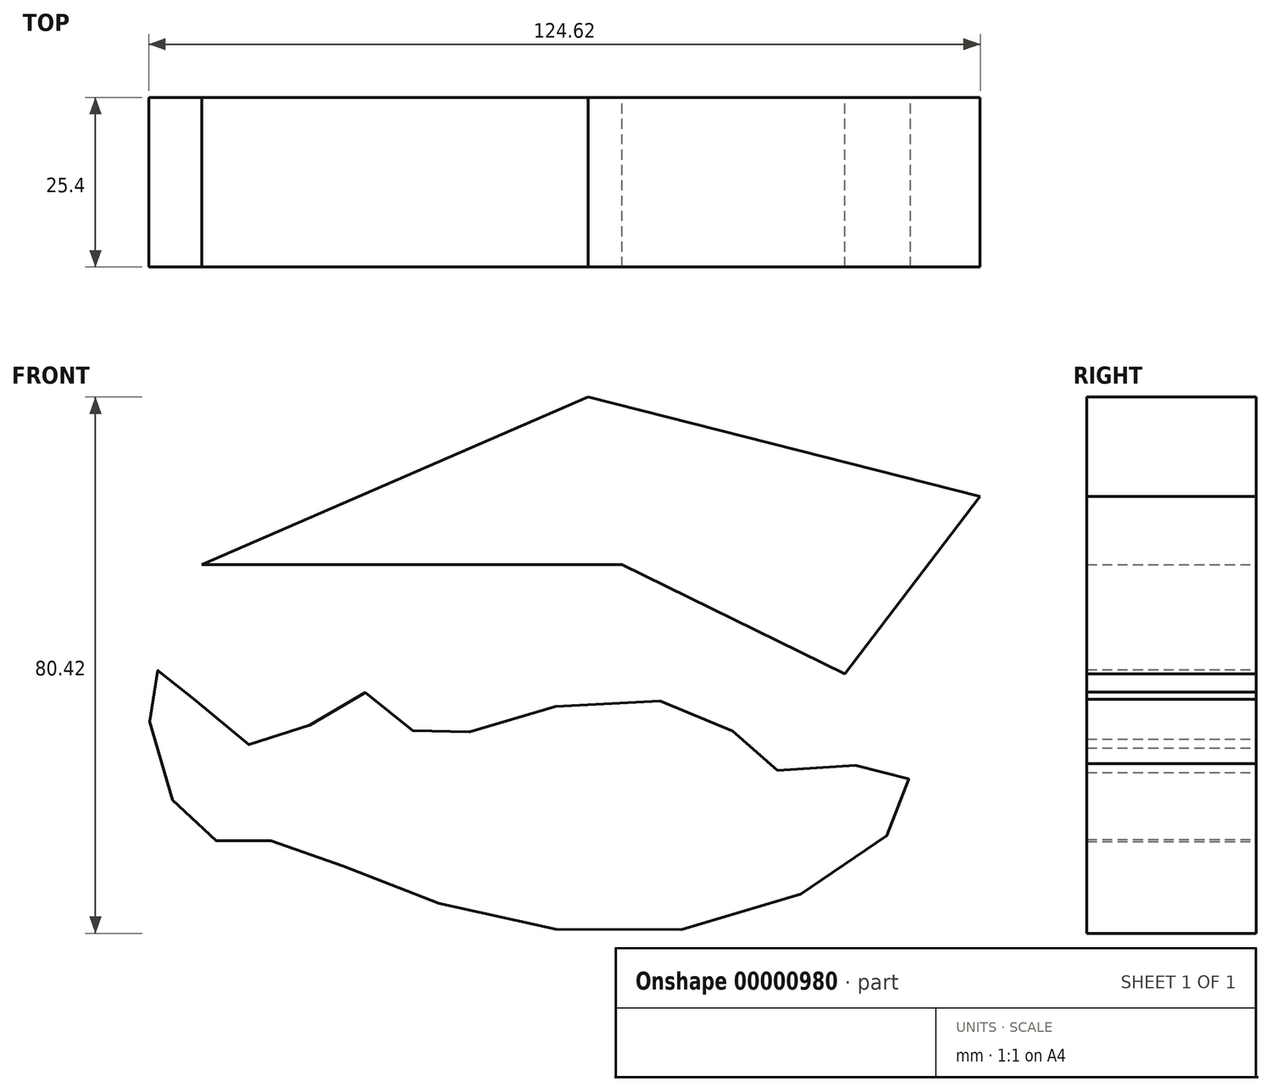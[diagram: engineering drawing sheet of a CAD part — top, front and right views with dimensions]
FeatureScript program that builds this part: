
annotation { "Feature Type Name" : "Feature", "Feature Type Description" : "" }
export const myFeature = defineFeature(function(context is Context, id is Id, definition is map)
    precondition{}
    {
        {
            var Q0;
            Q0=qCreatedBy(makeId("Front.planeOp"),FACE);
            var sketch = newSketch(context, id + "F0", { "sketchPlane" : qUnion([Q0])});
            skLineSegment(sketch, "E0", {"start": v(-57.86, 36.5) * mm, "end": v(5.1, 36.5) * mm});
            skLineSegment(sketch, "E1", {"start": v(5.1, 36.5) * mm, "end": v(38.54, 20.14) * mm});
            skLineSegment(sketch, "E2", {"start": v(38.54, 20.14) * mm, "end": v(58.8, 46.74) * mm});
            skLineSegment(sketch, "E3", {"start": v(58.8, 46.74) * mm, "end": v(0, 61.63) * mm});
            skLineSegment(sketch, "E4", {"start": v(0, 61.63) * mm, "end": v(-57.86, 36.5) * mm});
            skFitSpline(sketch, "E5", {"points": [v(-59.03, 16.3) * mm, v(-47.07, 9.13) * mm, v(-34.24, 17.4) * mm, v(-25.11, 10.87) * mm, v(-10.54, 13.91) * mm, v(19.02, 13.7) * mm, v(28.37, 5.65) * mm, v(45.98, 6.3) * mm, v(47.72, 0) * mm, v(18.8, -17.4) * mm, v(-27.29, -12.61) * mm, v(-48.6, -4.78) * mm, v(-57.5, -4.35) * mm, v(-65.33, 10.44) * mm, v(-64.46, 20.65) * mm, v(-59.03, 16.3) * mm]});
            skSolve(sketch);
        }
        {
            var Q0;
            Q0=makeQuery(id+"F0.imprint","IMPRINT",FACE,{"disambiguationData":[TD([[makeQuery(id+"F0.imprint","IMPRINT",EDGE,{"derivedFrom":sQuery(id+"F0.wireOp",EDGE,"E0")}),1.0]])]});
            var Q1;
            Q1=makeQuery(id+"F0.imprint","IMPRINT",FACE,{"disambiguationData":[TD([[makeQuery(id+"F0.imprint","IMPRINT",EDGE,{"derivedFrom":sQuery(id+"F0.wireOp",EDGE,"E5")}),-1.0]])]});
            extrude(context, id + "F1", {"entities" : qUnion([Q0, Q1]), "depth" : 25.4 * mm});
        }
    });
